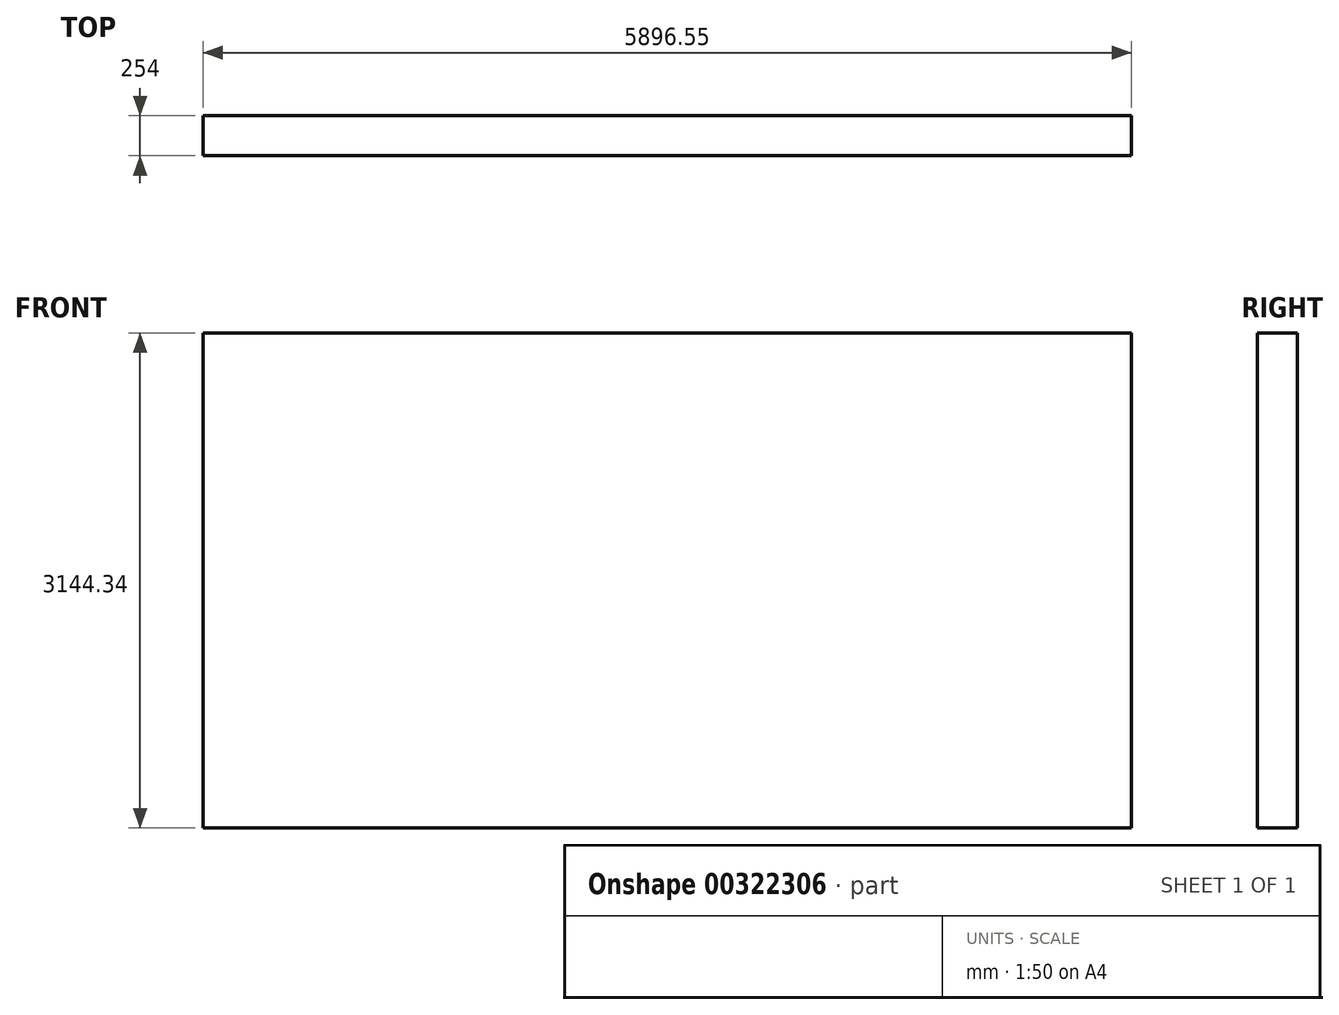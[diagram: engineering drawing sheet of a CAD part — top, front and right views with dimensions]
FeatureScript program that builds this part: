
annotation { "Feature Type Name" : "Feature", "Feature Type Description" : "" }
export const myFeature = defineFeature(function(context is Context, id is Id, definition is map)
    precondition{}
    {
        {
            var Q0;
            Q0=qCreatedBy(makeId("Front.planeOp"),FACE);
            var sketch = newSketch(context, id + "F0", { "sketchPlane" : qUnion([Q0])});
            skLineSegment(sketch, "E0.bottom", {"start": v(-269.28, -71.34) * mm, "end": v(-163.93, -71.34) * mm});
            skLineSegment(sketch, "E0.top", {"start": v(-269.28, -167.68) * mm, "end": v(-163.93, -167.68) * mm});
            skLineSegment(sketch, "E0.left", {"start": v(-269.28, -71.34) * mm, "end": v(-269.28, -167.68) * mm});
            skLineSegment(sketch, "E0.right", {"start": v(-163.93, -71.34) * mm, "end": v(-163.93, -167.68) * mm});
            skSolve(sketch);
        }
        {
            var Q0;
            Q0 = qSketchRegion(id + "F0", true);
            extrude(context, id + "F1", {"entities" : qUnion([Q0]), "depth" : 254 * mm});
        }
        {
            var Q0;
            Q0=makeQuery(id+"F1.opExtrude","SWEPT_FACE",FACE,{"disambiguationData":[OSD([sQuery(id+"F0.wireOp",EDGE,"E0.bottom")])]});
            extrude(context, id + "F2", {"entities" : qUnion([Q0]), "operationType" : NewBodyOperationType.ADD, "depth" : 254 * mm});
        }
        {
            var Q0;
            {var subQ0=sQuery(id+"F0.wireOp",EDGE,"E0.right");Q0=makeQuery(id+"F2.boolean.opBoolean","MERGE",FACE,{"derivedFrom":[makeQuery(id+"F1.opExtrude","SWEPT_FACE",FACE,{"disambiguationData":[OSD([subQ0])]}),makeQuery(id+"F2.opExtrude","SWEPT_FACE",FACE,{"disambiguationData":[OSD([sQuery(id+"F0.wireOp",EDGE,"E0.bottom"),subQ0])]})]});}
            extrude(context, id + "F3", {"entities" : qUnion([Q0]), "operationType" : NewBodyOperationType.ADD, "depth" : 508 * mm});
        }
        {
            var Q0;
            {var subQ0=sQuery(id+"F0.wireOp",EDGE,"E0.left");Q0=makeQuery(id+"F2.boolean.opBoolean","MERGE",FACE,{"derivedFrom":[makeQuery(id+"F1.opExtrude","SWEPT_FACE",FACE,{"disambiguationData":[OSD([subQ0])]}),makeQuery(id+"F2.opExtrude","SWEPT_FACE",FACE,{"disambiguationData":[OSD([sQuery(id+"F0.wireOp",EDGE,"E0.bottom"),subQ0])]})]});}
            var sketch = newSketch(context, id + "F4", { "sketchPlane" : qUnion([Q0])});
            skSolve(sketch);
        }
        {
            var Q0;
            {var subQ0=sQuery(id+"F0.wireOp",EDGE,"E0.left");Q0=makeQuery(id+"F4.imprint","IMPRINT",FACE,{"disambiguationData":[TD([[makeQuery(id+"F4.imprint","IMPRINT",EDGE,{"derivedFrom":makeQuery(id+"F1.opExtrude","SWEPT_EDGE",EDGE,{"disambiguationData":[OSD([sQuery(id+"F0.wireOp",EDGE,"E0.top"),subQ0])]})}),-1.0]])]});}
            extrude(context, id + "F5", {"entities" : qUnion([Q0]), "operationType" : NewBodyOperationType.ADD, "depth" : 762 * mm});
        }
        {
            var Q0;
            {var subQ0=sQuery(id+"F0.wireOp",EDGE,"E0.top");Q0=makeQuery(id+"F5.boolean.opBoolean","MERGE",FACE,{"derivedFrom":[makeQuery(id+"F3.boolean.opBoolean","MERGE",FACE,{"derivedFrom":[makeQuery(id+"F1.opExtrude","SWEPT_FACE",FACE,{"disambiguationData":[OSD([subQ0])]}),makeQuery(id+"F3.opExtrude","SWEPT_FACE",FACE,{"disambiguationData":[OSD([subQ0,sQuery(id+"F0.wireOp",EDGE,"E0.right")])]})]}),makeQuery(id+"F5.opExtrude","SWEPT_FACE",FACE,{"disambiguationData":[OSD([subQ0,sQuery(id+"F0.wireOp",EDGE,"E0.left")])]})]});}
            extrude(context, id + "F6", {"entities" : qUnion([Q0]), "operationType" : NewBodyOperationType.ADD, "depth" : 254 * mm});
        }
        {
            var Q0;
            {var subQ0=sQuery(id+"F0.wireOp",EDGE,"E0.left");var subQ1=sQuery(id+"F0.wireOp",EDGE,"E0.top");Q0=makeQuery(id+"F6.boolean.opBoolean","MERGE",FACE,{"derivedFrom":[makeQuery(id+"F5.opExtrude","CAP_FACE",FACE,{"disambiguationData":[OSD([sQuery(id+"F0.wireOp",EDGE,"E0.bottom"),subQ1,subQ0])],"isStart":false}),makeQuery(id+"F6.opExtrude","SWEPT_FACE",FACE,{"disambiguationData":[OSD([subQ1,subQ0])]})]});}
            extrude(context, id + "F7", {"entities" : qUnion([Q0]), "operationType" : NewBodyOperationType.ADD, "depth" : 584.2 * mm});
        }
        {
            var Q0;
            Q0=makeQuery(id+"F7.opExtrude","CAP_FACE",FACE,{"disambiguationData":[OSD([sQuery(id+"F0.wireOp",EDGE,"E0.bottom"),sQuery(id+"F0.wireOp",EDGE,"E0.top"),sQuery(id+"F0.wireOp",EDGE,"E0.left")])],"isStart":false});
            extrude(context, id + "F8", {"entities" : qUnion([Q0]), "operationType" : NewBodyOperationType.ADD, "depth" : 3937 * mm});
        }
        {
            var Q0;
            {var subQ0=sQuery(id+"F0.wireOp",EDGE,"E0.left");var subQ1=sQuery(id+"F0.wireOp",EDGE,"E0.bottom");var subQ2=sQuery(id+"F0.wireOp",EDGE,"E0.right");Q0=makeQuery(id+"F8.boolean.opBoolean","MERGE",FACE,{"derivedFrom":[makeQuery(id+"F7.boolean.opBoolean","MERGE",FACE,{"derivedFrom":[makeQuery(id+"F5.boolean.opBoolean","MERGE",FACE,{"derivedFrom":[makeQuery(id+"F3.boolean.opBoolean","MERGE",FACE,{"derivedFrom":[makeQuery(id+"F2.opExtrude","CAP_FACE",FACE,{"disambiguationData":[OSD([subQ1])],"isStart":false}),makeQuery(id+"F3.opExtrude","SWEPT_FACE",FACE,{"disambiguationData":[OSD([subQ1,subQ2]),TDD([makeQuery(id+"F2.opExtrude","CAP_EDGE",EDGE,{"disambiguationData":[OSD([subQ1,subQ2])],"isStart":false})])]})]}),makeQuery(id+"F5.opExtrude","SWEPT_FACE",FACE,{"disambiguationData":[OSD([subQ1,subQ0]),TDD([makeQuery(id+"F4.imprint","IMPRINT",EDGE,{"derivedFrom":makeQuery(id+"F2.opExtrude","CAP_EDGE",EDGE,{"disambiguationData":[OSD([subQ1,subQ0])],"isStart":false})})])]})]}),makeQuery(id+"F7.opExtrude","SWEPT_FACE",FACE,{"disambiguationData":[OSD([subQ1,subQ0])]})]}),makeQuery(id+"F8.opExtrude","SWEPT_FACE",FACE,{"disambiguationData":[OSD([subQ1,subQ0])]})]});}
            extrude(context, id + "F9", {"entities" : qUnion([Q0]), "operationType" : NewBodyOperationType.ADD, "depth" : 2540 * mm});
        }
    });
